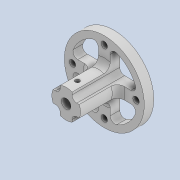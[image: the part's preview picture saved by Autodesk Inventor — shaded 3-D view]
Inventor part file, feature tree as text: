
AUTODESK INVENTOR PART (.ipt)
format: ipt  version: 2020 (Build 240168000, 168)  size: 257,024 bytes
history: native  units: mm
features: thicken_offset x4, other x4, extrude x3, sketch x3, projected_geometry x2, fillet x1, reference x1
ambient origin geometry x8: Origin, YZ Plane, XZ Plane, XY Plane, X Axis, Y Axis, Z Axis, Center Point
bodies: Solid1 (feature_tree)
feature tree (18):
  extrude  "Extrusion1"  Depth=3.0mm TaperAngle=0.0deg
  extrude  "Extrusion2"  Depth=12.0mm TaperAngle=0.0deg
  fillet  "Fillet1"  Radius=2.0mm
  thicken_offset  "Thicken1"
  thicken_offset  "Thicken2"
  thicken_offset  "Thicken3"
  thicken_offset  "Thicken4"
  extrude  "Extrusion3"  Depth=1.0mm
  sketch  "Sketch1"  dims[d0=3.0mm d1=3.0mm d2=0.0mm]
  reference  "Reference1"
  sketch  "Sketch2"  dims[d3=3.0mm d4=12.0mm d5=0.0mm d6=2.0mm]
  projected_geometry  "Projected Loop1"
  sketch  "Sketch3"  dims[d7=1.0mm d8=1.0mm d9=1.0mm d10=1.0mm d11=1.0mm d12=1.0mm d13=1.0mm d14=1.0mm d15=3.5mm d16=1.4mm d17=12.0mm d18=0.0mm]
  projected_geometry  "Projected Loop2"
  parser-record x1  (decoder bookkeeping rows leaked as tree rows — omitted from the tree; the rows remain in map.json)
  other  "tip_3_ass_base.iam"
  other  "mot_27_ass:1"
  other  "mot_27_1:1"
note: 1 file-system path scrubbed to <path> (originals preserved in map.json)
